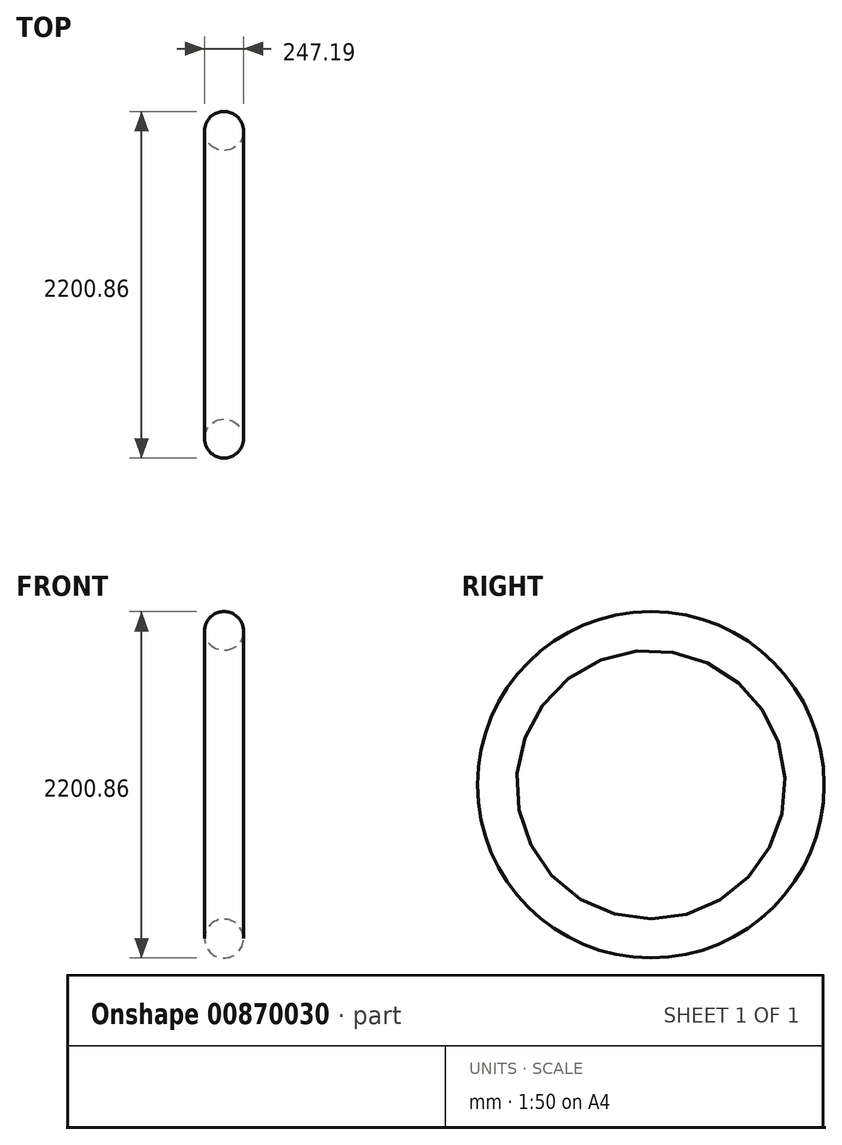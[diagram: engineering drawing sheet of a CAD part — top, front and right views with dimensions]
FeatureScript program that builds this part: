
annotation { "Feature Type Name" : "Feature", "Feature Type Description" : "" }
export const myFeature = defineFeature(function(context is Context, id is Id, definition is map)
    precondition{}
    {
        {
            var Q0;
            Q0=qCreatedBy(makeId("Front.planeOp"),FACE);
            var sketch = newSketch(context, id + "F0", { "sketchPlane" : qUnion([Q0])});
            skCircle(sketch, "E0", {"center": v(14.4, 0) * mm, "radius": 123.6 * mm});
            skSolve(sketch);
        }
        {
            var Q0;
            Q0=makeQuery(id+"F0.imprint","IMPRINT",FACE,{"disambiguationData":[TD([[makeQuery(id+"F0.imprint","IMPRINT",EDGE,{"derivedFrom":sQuery(id+"F0.wireOp",EDGE,"E0")}),1.0]])]});
            var sketch = newSketch(context, id + "F1", { "sketchPlane" : qUnion([Q0])});
            skLineSegment(sketch, "E1", {"start": v(-172.91, 976.84) * mm, "end": v(436.14, 976.84) * mm});
            skSolve(sketch);
        }
        {
            var Q0;
            Q0=sQuery(id+"F0.wireOp",EDGE,"E0");
            var Q1;
            Q1=sQuery(id+"F1.wireOp",EDGE,"E1");
            revolve(context, id + "F2", {"bodyType" : ToolBodyType.SURFACE, "surfaceOperationType" : NewSurfaceOperationType.NEW, "surfaceEntities" : qUnion([Q0]), "axis" : qUnion([Q1]), "revolveType" : RevolveType.FULL});
        }
    });
